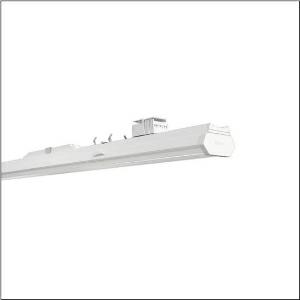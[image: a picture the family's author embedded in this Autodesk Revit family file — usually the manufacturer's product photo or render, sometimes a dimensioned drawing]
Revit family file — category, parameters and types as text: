
# Revit family: licross_r__11_protected_mo_51tp12dn495g_6914
name_source: partatom
category: Lighting Fixtures
units: mm (PartAtom-declared; Revit-internal decimal feet)

## family parameters
Cut with Voids When Loaded = No
Host = Face
Light Source = No
Part Type = Normal
Room Calculation Point = No
Round Connector Dimension = Use Diameter
Shared = No

## types (1)
- --- (1 x LED, 9980 lm, 57.1 W, 4000K)
    Apparent Load = 57 VA
    CIE Flux Codes = 73 92 98 99 100
    Color Rendering = 80
    Color Temperature = 4000K
    Default Elevation = 1800 mm
    Description = Licross® 11 Protected MO, luminaire insert, of sheet steel, galvanised, coil coated, white, length: 1.500mm, width: 90mm, height: 101mm, LED rated luminous flux: 9.980lm, light colour: 840, control gear: DALI 2, control gear: ECG DALI, with plug, 5-pole, with phase selection, mains connection: 220..240V, AC, 50/60Hz, halogen-free wiring, primary optical cover: cover, of PMMA, light emission: direct with ceiling illumination distribution, primary light characteristic: symmetric, protection rating (complete): IP64, insulation class (complete): insulation class I (protective earthing), certification: CE, ENEC, VDE, UKCA, protection symbol: D if used in an environment with conductive dust loads with corresponding accessories, impact resistance: IK06, permissible ambient temperature for indoor applications: -25..+35°C, corresponds to IFS (International Featured Standards) requirements for safety and quality in the food industry, reducing of maximum allowable ambient temperature of 5°C with ceiling mounting, LABS conformity tested according to VDMA 24364:2018-05, packaging unit: 1 piece
    Height = 92 mm
    Lamp = 1 x LED
    Lamp Light Flux = 9980 lm
    Lamp Power = 57.1 W
    Lamp count = 1
    Length = 1500 mm
    Luminous efficacy = 175 lm/W
    Manufacturer = Siteco
    ModVariant = No
    Model = 51TP12DN495G
    Mounting Place = Ceiling
    Mounting Type = Pendant
    Number of Poles = 1
    OnlyDefault = Yes
    Power Factor = 1
    Product Name = Licross® 11 Protected MO
    Product group = luminaire insert
    ProductGroupID = 902
    Protection Class = Protection class I
    Protection Degree = IP 64
    RLX_Detail_Level = 1
    RlxData = <blob elided: 24493 chars, md5=64cf193b>
    Socket = socket
    Standby Power = 0 W
    System Light Flux = 9980 lm
    System Power = 57 W
    Type Comments = factory setting: luminous flux: 100 % | dim-lin: 254 | 378 mA
    Type Image = l_1256148.jpg
    URL = http://relux.com
    VarID = @adj_010249
    Voltage = 0 V
    Weight = 0.00 kg
    Width = 88 mm

## geometry (parser evidence)
native form markers: Blend x4, Sweep x9
no freeform markers — native parametric forms only
